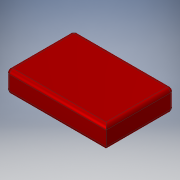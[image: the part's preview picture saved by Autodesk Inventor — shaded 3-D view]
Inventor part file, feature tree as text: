
AUTODESK INVENTOR PART (.ipt)
format: ipt  version: 2017.3 (Build 213257000, 257)  size: 137,728 bytes
history: native  units: mm
features: fillet x2, extrude x1, sketch x1
ambient origin geometry x8: Origin, YZ Plane, XZ Plane, XY Plane, X Axis, Y Axis, Z Axis, Center Point
bodies: Volumenkörper1 (feature_tree)
feature tree (4):
  extrude  "Extrusion1"  Depth=19.0mm
  fillet  "Rundung1"  Radius=6.0mm
  fillet  "Rundung2"  Radius=1.0mm
  sketch  "Skizze1"  dims[d0=28.0mm d1=19.0mm d2=6.0mm d3=0.0mm d4=1.0mm d5=1.0mm]
